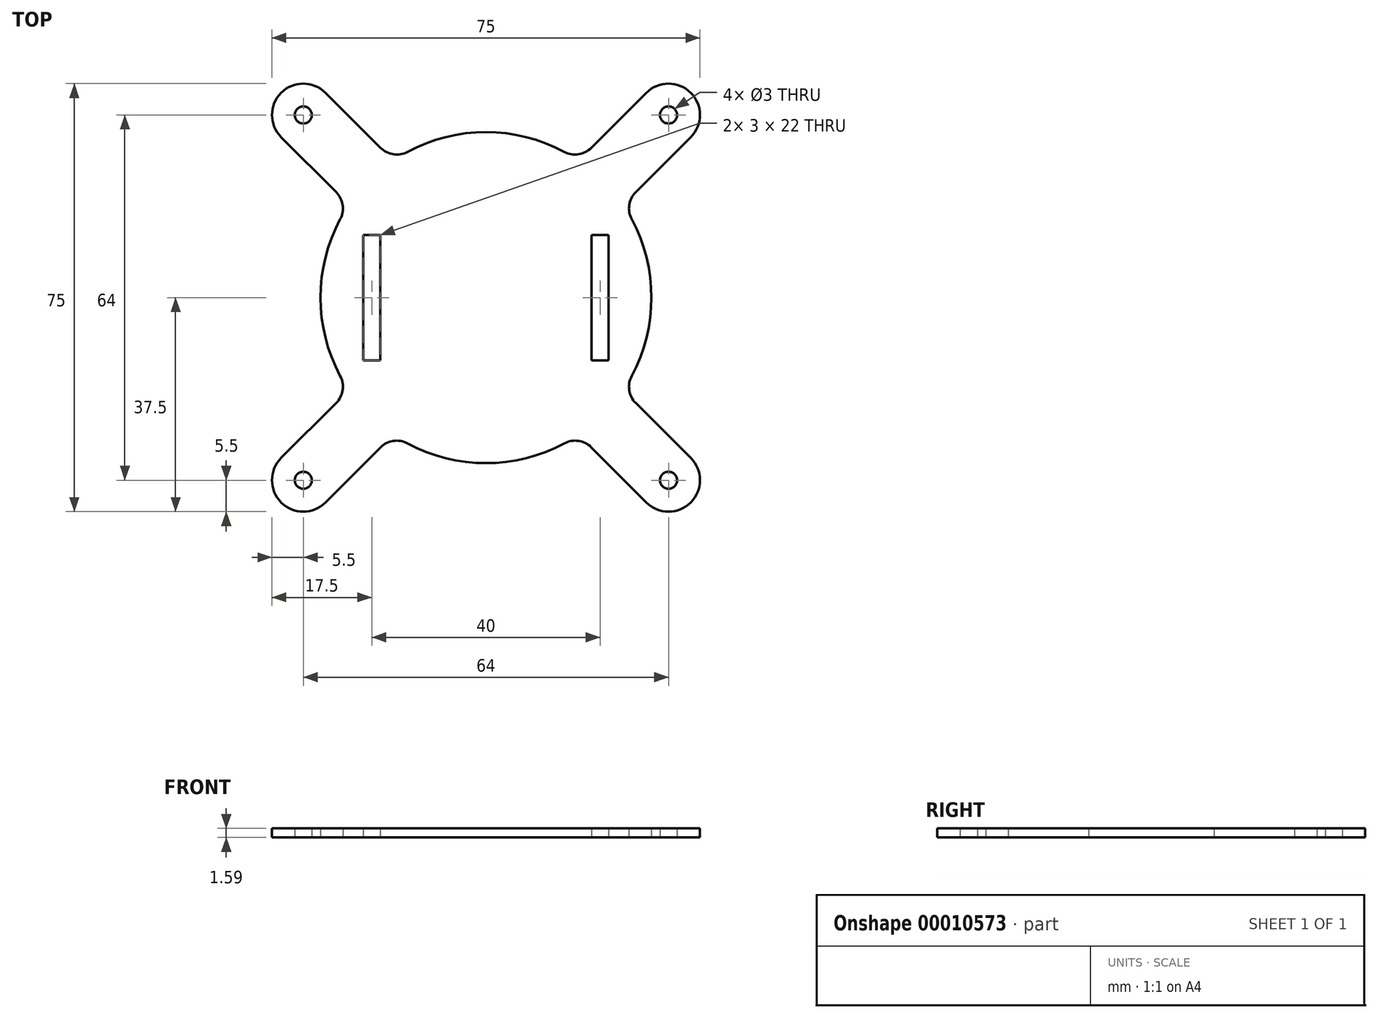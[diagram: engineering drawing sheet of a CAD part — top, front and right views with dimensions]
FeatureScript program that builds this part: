
annotation { "Feature Type Name" : "Feature", "Feature Type Description" : "" }
export const myFeature = defineFeature(function(context is Context, id is Id, definition is map)
    precondition{}
    {
        {
            var Q0;
            Q0=qCreatedBy(makeId("Top.planeOp"),FACE);
            var sketch = newSketch(context, id + "F0", { "sketchPlane" : qUnion([Q0])});
            skCircle(sketch, "E0", {"center": v(-32, -32) * mm, "radius": 1.5 * mm});
            skCircle(sketch, "E1", {"center": v(-32, 32) * mm, "radius": 1.5 * mm});
            skCircle(sketch, "E2", {"center": v(32, 32) * mm, "radius": 1.5 * mm});
            skCircle(sketch, "E3", {"center": v(32, -32) * mm, "radius": 1.5 * mm});
            skLineSegment(sketch, "E4", {"start": v(-32, 32) * mm, "end": v(-32, -32) * mm, "construction": true});
            skLineSegment(sketch, "E5", {"start": v(-32, -32) * mm, "end": v(32, -32) * mm, "construction": true});
            skLineSegment(sketch, "E6", {"start": v(-32, 32) * mm, "end": v(32, 32) * mm, "construction": true});
            skLineSegment(sketch, "E7", {"start": v(32, -32) * mm, "end": v(32, 32) * mm, "construction": true});
            skCircle(sketch, "E8.0", {"center": v(0, 0) * mm, "radius": 29 * mm});
            skCircle(sketch, "E9.0", {"center": v(-32, 32) * mm, "radius": 5.5 * mm});
            skLineSegment(sketch, "E10", {"start": v(-35.89, 28.11) * mm, "end": v(-24.02, 16.24) * mm});
            skLineSegment(sketch, "E11", {"start": v(-28.11, 35.89) * mm, "end": v(-16.24, 24.02) * mm});
            skLineSegment(sketch, "E12", {"start": v(0, 0) * mm, "end": v(-32, 32) * mm, "construction": true});
            skCircle(sketch, "E13", {"center": v(32, 32) * mm, "radius": 5.5 * mm});
            skCircle(sketch, "E14", {"center": v(32, -32) * mm, "radius": 5.5 * mm});
            skCircle(sketch, "E15", {"center": v(-32, -32) * mm, "radius": 5.5 * mm});
            skLineSegment(sketch, "E16", {"start": v(0, 0) * mm, "end": v(32, 32) * mm, "construction": true});
            skLineSegment(sketch, "E17", {"start": v(0, 0) * mm, "end": v(32, -32) * mm, "construction": true});
            skLineSegment(sketch, "E18", {"start": v(0, 0) * mm, "end": v(-32, -32) * mm, "construction": true});
            skLineSegment(sketch, "E19", {"start": v(-35.89, -28.11) * mm, "end": v(-24.02, -16.24) * mm});
            skLineSegment(sketch, "E20", {"start": v(-28.11, -35.89) * mm, "end": v(-16.24, -24.02) * mm});
            skLineSegment(sketch, "E21", {"start": v(28.11, -35.89) * mm, "end": v(16.24, -24.02) * mm});
            skLineSegment(sketch, "E22", {"start": v(35.89, -28.11) * mm, "end": v(24.02, -16.24) * mm});
            skLineSegment(sketch, "E23", {"start": v(35.89, 28.11) * mm, "end": v(24.02, 16.24) * mm});
            skLineSegment(sketch, "E24", {"start": v(28.11, 35.89) * mm, "end": v(16.24, 24.02) * mm});
            skLineSegment(sketch, "E25.rect.bottom", {"start": v(21.5, 11) * mm, "end": v(18.5, 11) * mm});
            skLineSegment(sketch, "E25.rect.top", {"start": v(21.5, -11) * mm, "end": v(18.5, -11) * mm});
            skLineSegment(sketch, "E25.rect.left", {"start": v(21.5, 11) * mm, "end": v(21.5, -11) * mm});
            skLineSegment(sketch, "E25.rect.right", {"start": v(18.5, 11) * mm, "end": v(18.5, -11) * mm});
            skPoint(sketch, "E25.rect.middle", {"position": v(20, 0) * mm});
            skLineSegment(sketch, "E26.rect.bottom", {"start": v(-18.5, 11) * mm, "end": v(-21.5, 11) * mm});
            skLineSegment(sketch, "E26.rect.top", {"start": v(-18.5, -11) * mm, "end": v(-21.5, -11) * mm});
            skLineSegment(sketch, "E26.rect.left", {"start": v(-18.5, 11) * mm, "end": v(-18.5, -11) * mm});
            skLineSegment(sketch, "E26.rect.right", {"start": v(-21.5, 11) * mm, "end": v(-21.5, -11) * mm});
            skPoint(sketch, "E26.rect.middle", {"position": v(-20, 0) * mm});
            skLineSegment(sketch, "E27", {"start": v(-20, 0) * mm, "end": v(20, 0) * mm, "construction": true});
            skSolve(sketch);
        }
        {
            var Q0;
            Q0=makeQuery(id+"F0.imprint","IMPRINT",FACE,{"disambiguationData":[TD([[makeQuery(id+"F0.imprint","IMPRINT",EDGE,{"derivedFrom":sQuery(id+"F0.wireOp",EDGE,"5ebcd753-58cf-41b8-9fe7-78018a09ebfe")}),-1.0]])]});
            var Q1;
            {var subQ1=sQuery(id+"F0.wireOp",EDGE,"E19");Q1=makeQuery(id+"F0.imprint","IMPRINT",FACE,{"disambiguationData":[TD([[makeQuery(id+"F0.imprint","IMPRINT",EDGE,{"derivedFrom":subQ1}),-1.0]])]});}
            var Q2;
            {var subQ1=sQuery(id+"F0.wireOp",EDGE,"E21");Q2=makeQuery(id+"F0.imprint","IMPRINT",FACE,{"disambiguationData":[TD([[makeQuery(id+"F0.imprint","IMPRINT",EDGE,{"derivedFrom":subQ1}),-1.0]])]});}
            var Q3;
            {var subQ1=sQuery(id+"F0.wireOp",EDGE,"E23");Q3=makeQuery(id+"F0.imprint","IMPRINT",FACE,{"disambiguationData":[TD([[makeQuery(id+"F0.imprint","IMPRINT",EDGE,{"derivedFrom":subQ1}),-1.0]])]});}
            var Q4;
            Q4=makeQuery(id+"F0.imprint","IMPRINT",FACE,{"disambiguationData":[TD([[makeQuery(id+"F0.imprint","IMPRINT",EDGE,{"derivedFrom":sQuery(id+"F0.wireOp",EDGE,"E0")}),-1.0]])]});
            var Q5;
            Q5=makeQuery(id+"F0.imprint","IMPRINT",FACE,{"disambiguationData":[TD([[makeQuery(id+"F0.imprint","IMPRINT",EDGE,{"derivedFrom":sQuery(id+"F0.wireOp",EDGE,"E3")}),-1.0]])]});
            var Q6;
            Q6=makeQuery(id+"F0.imprint","IMPRINT",FACE,{"disambiguationData":[TD([[makeQuery(id+"F0.imprint","IMPRINT",EDGE,{"derivedFrom":sQuery(id+"F0.wireOp",EDGE,"E2")}),-1.0]])]});
            var Q7;
            Q7=makeQuery(id+"F0.imprint","IMPRINT",FACE,{"disambiguationData":[TD([[makeQuery(id+"F0.imprint","IMPRINT",EDGE,{"derivedFrom":sQuery(id+"F0.wireOp",EDGE,"E1")}),-1.0]])]});
            var Q8;
            {var subQ1=sQuery(id+"F0.wireOp",EDGE,"E10");Q8=makeQuery(id+"F0.imprint","IMPRINT",FACE,{"disambiguationData":[TD([[makeQuery(id+"F0.imprint","IMPRINT",EDGE,{"derivedFrom":subQ1}),1.0]])]});}
            var Q9;
            {var subQ4=sQuery(id+"F0.wireOp",EDGE,"E25.rect.right");Q9=makeQuery(id+"F0.imprint","IMPRINT",FACE,{"disambiguationData":[TD([[makeQuery(id+"F0.imprint","IMPRINT",EDGE,{"derivedFrom":subQ4}),-1.0]])]});}
            var Q10;
            {var subQ1=sQuery(id+"F0.wireOp",EDGE,"5ebcd753-58cf-41b8-9fe7-78018a09ebfe");var subQ11=sQuery(id+"F0.wireOp",EDGE,"3e3f14dc-ae8a-4fa7-b69b-edc12a99b693.rect.left");var subQ13=makeQuery(id+"F0.imprint","INTERSECT",VERTEX,{"derivedFrom":[subQ1,subQ11]});Q10=makeQuery(id+"F0.imprint","IMPRINT",FACE,{"disambiguationData":[TD([[makeQuery(id+"F0.imprint","IMPRINT",EDGE,{"disambiguationData":[TD([[subQ13,-1.0]])],"derivedFrom":subQ1}),-1.0]])]});}
            var Q11;
            {var subQ0=sQuery(id+"F0.wireOp",EDGE,"a991359a-60d6-44f3-9616-c6d5c296645e.rect.right");var subQ1=sQuery(id+"F0.wireOp",EDGE,"5ebcd753-58cf-41b8-9fe7-78018a09ebfe");var subQ2=makeQuery(id+"F0.imprint","INTERSECT",VERTEX,{"derivedFrom":[subQ1,subQ0]});Q11=makeQuery(id+"F0.imprint","IMPRINT",FACE,{"disambiguationData":[TD([[makeQuery(id+"F0.imprint","IMPRINT",EDGE,{"disambiguationData":[TD([[subQ2,-1.0]])],"derivedFrom":subQ1}),-1.0]])]});}
            extrude(context, id + "F1", {"entities" : qUnion([Q0, Q1, Q2, Q3, Q4, Q5, Q6, Q7, Q8, Q9, Q10, Q11]), "depth" : 1.59 * mm});
        }
        {
            var Q0;
            Q0=makeQuery(id+"F1.opExtrude","SWEPT_EDGE",EDGE,{"disambiguationData":[OSD([sQuery(id+"F0.wireOp",EDGE,"E8.0"),sQuery(id+"F0.wireOp",EDGE,"E20")])]});
            var Q1;
            Q1=makeQuery(id+"F1.opExtrude","SWEPT_EDGE",EDGE,{"disambiguationData":[OSD([sQuery(id+"F0.wireOp",EDGE,"E8.0"),sQuery(id+"F0.wireOp",EDGE,"E21")])]});
            var Q2;
            Q2=makeQuery(id+"F1.opExtrude","SWEPT_EDGE",EDGE,{"disambiguationData":[OSD([sQuery(id+"F0.wireOp",EDGE,"E8.0"),sQuery(id+"F0.wireOp",EDGE,"E22")])]});
            var Q3;
            Q3=makeQuery(id+"F1.opExtrude","SWEPT_EDGE",EDGE,{"disambiguationData":[OSD([sQuery(id+"F0.wireOp",EDGE,"E8.0"),sQuery(id+"F0.wireOp",EDGE,"E23")])]});
            var Q4;
            Q4=makeQuery(id+"F1.opExtrude","SWEPT_EDGE",EDGE,{"disambiguationData":[OSD([sQuery(id+"F0.wireOp",EDGE,"E8.0"),sQuery(id+"F0.wireOp",EDGE,"E24")])]});
            var Q5;
            Q5=makeQuery(id+"F1.opExtrude","SWEPT_EDGE",EDGE,{"disambiguationData":[OSD([sQuery(id+"F0.wireOp",EDGE,"E8.0"),sQuery(id+"F0.wireOp",EDGE,"E11")])]});
            var Q6;
            Q6=makeQuery(id+"F1.opExtrude","SWEPT_EDGE",EDGE,{"disambiguationData":[OSD([sQuery(id+"F0.wireOp",EDGE,"E8.0"),sQuery(id+"F0.wireOp",EDGE,"E10")])]});
            var Q7;
            Q7=makeQuery(id+"F1.opExtrude","SWEPT_EDGE",EDGE,{"disambiguationData":[OSD([sQuery(id+"F0.wireOp",EDGE,"E8.0"),sQuery(id+"F0.wireOp",EDGE,"E19")])]});
            fillet(context, id + "F2", {"entities" : qUnion([Q0, Q1, Q2, Q3, Q4, Q5, Q6, Q7]), "radius" : 4 * mm, "tangentPropagation" : true, "allowEdgeOverflow" : false});
        }
    });
